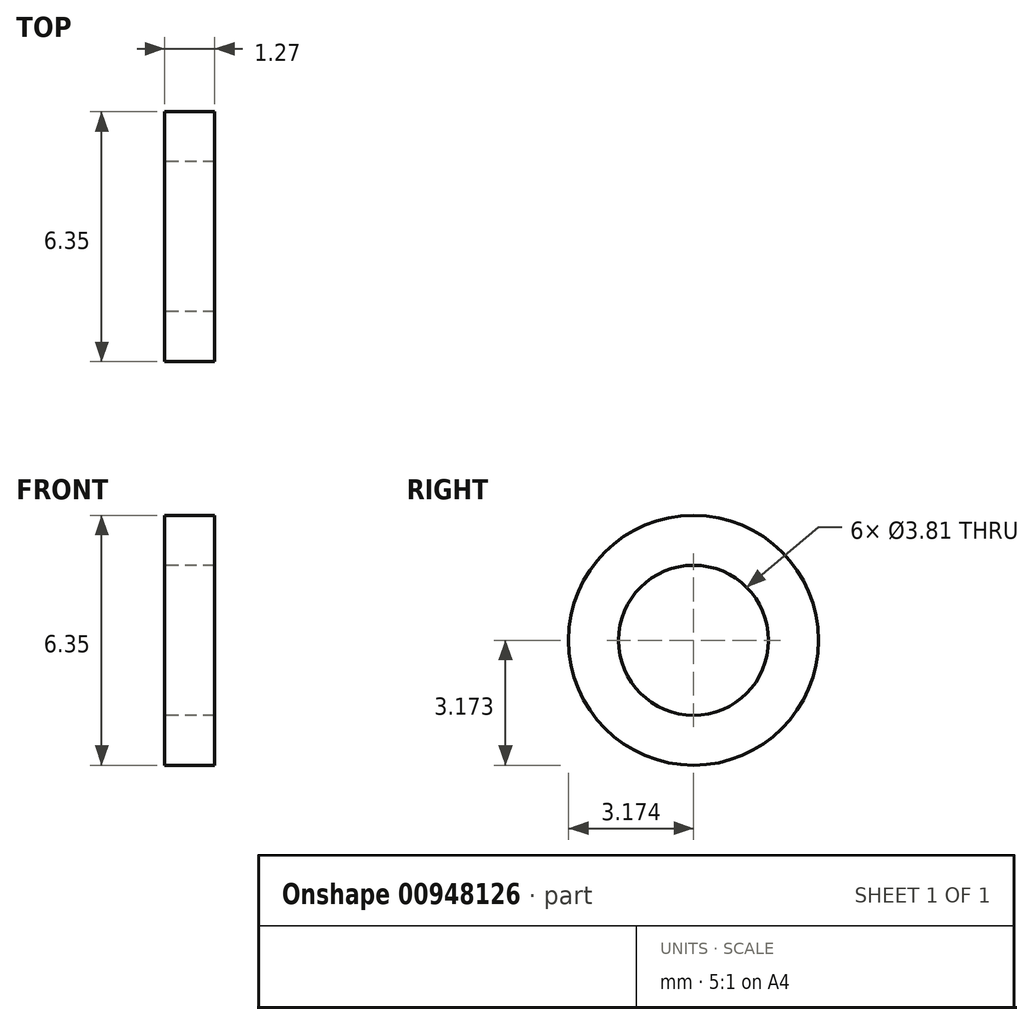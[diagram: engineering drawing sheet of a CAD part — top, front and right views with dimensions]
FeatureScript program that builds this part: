
annotation { "Feature Type Name" : "Feature", "Feature Type Description" : "" }
export const myFeature = defineFeature(function(context is Context, id is Id, definition is map)
    precondition{}
    {
        {
            var Q0;
            Q0=qCreatedBy(makeId("Right.planeOp"),FACE);
            var sketch = newSketch(context, id + "F0", { "sketchPlane" : qUnion([Q0])});
            skCircle(sketch, "E0", {"center": v(-21.55, 16) * mm, "radius": 3.18 * mm});
            skCircle(sketch, "E1", {"center": v(-21.55, 16) * mm, "radius": 1.9 * mm});
            skSolve(sketch);
        }
        {
            var Q0;
            Q0=makeQuery(id+"F0.imprint","IMPRINT",FACE,{"disambiguationData":[TD([[makeQuery(id+"F0.imprint","IMPRINT",EDGE,{"derivedFrom":sQuery(id+"F0.wireOp",EDGE,"E0")}),1.0]])]});
            extrude(context, id + "F1", {"entities" : qUnion([Q0]), "depth" : 1.27 * mm, "offsetDistance" : 25.4 * mm});
        }
    });
